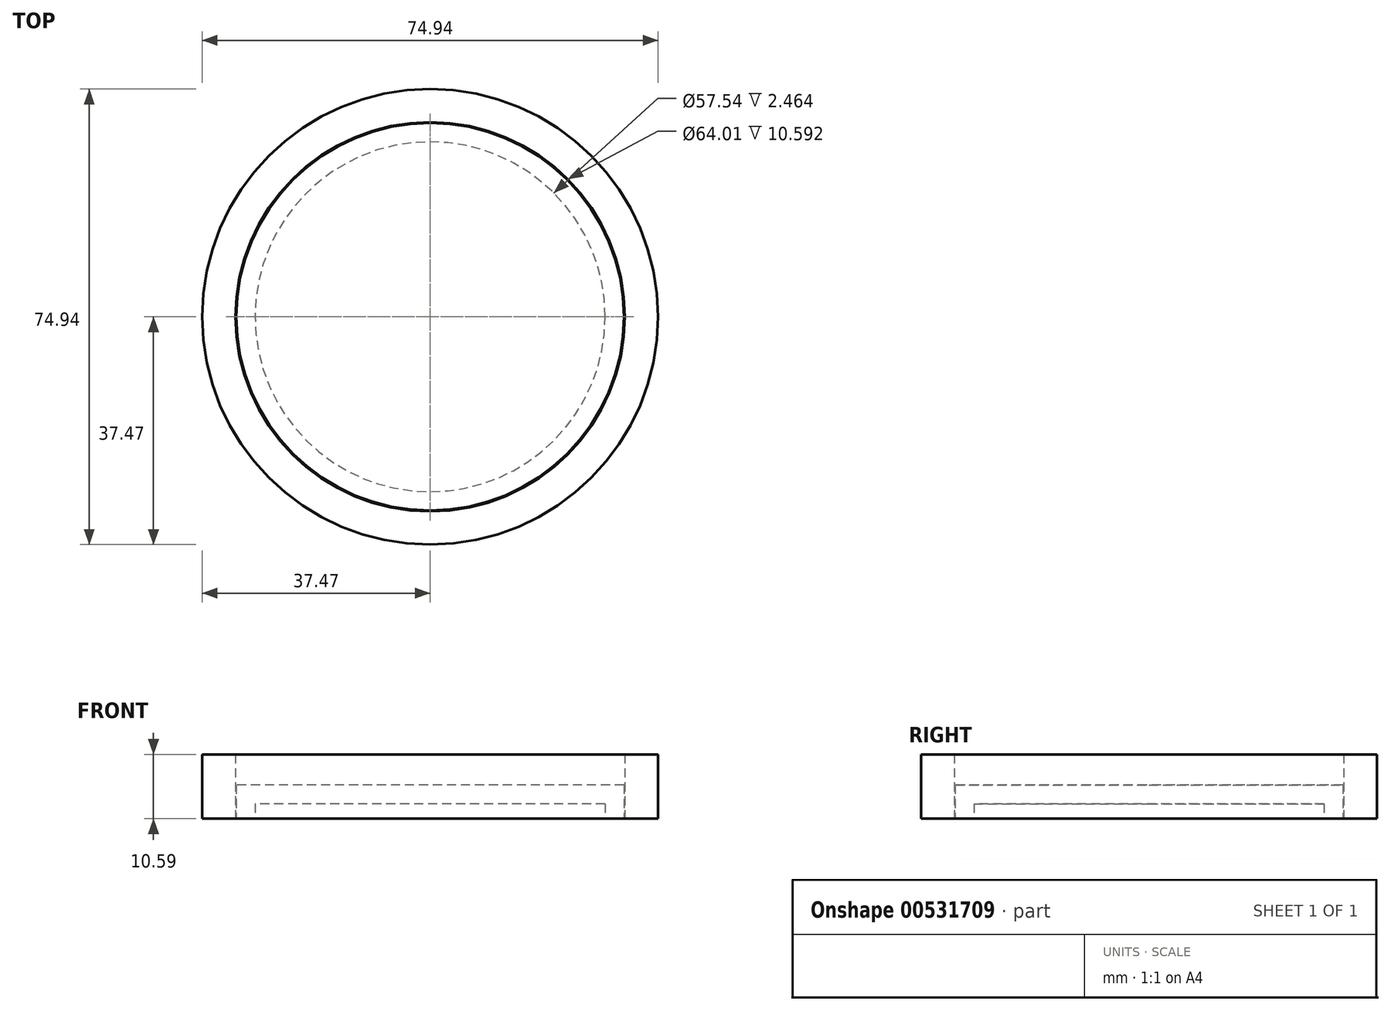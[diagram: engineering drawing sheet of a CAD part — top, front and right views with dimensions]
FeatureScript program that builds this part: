
annotation { "Feature Type Name" : "Feature", "Feature Type Description" : "" }
export const myFeature = defineFeature(function(context is Context, id is Id, definition is map)
    precondition{}
    {
        {
            var Q0;
            Q0=qCreatedBy(makeId("Top.planeOp"),FACE);
            var sketch = newSketch(context, id + "F0", { "sketchPlane" : qUnion([Q0])});
            skCircle(sketch, "E0", {"center": v(0, 0) * mm, "radius": 32 * mm});
            skCircle(sketch, "E1", {"center": v(0, 0) * mm, "radius": 37.47 * mm});
            skSolve(sketch);
        }
        {
            var Q0;
            Q0=makeQuery(id+"F0.imprint","IMPRINT",FACE,{"disambiguationData":[TD([[makeQuery(id+"F0.imprint","IMPRINT",EDGE,{"derivedFrom":sQuery(id+"F0.wireOp",EDGE,"E0")}),-1.0]])]});
            extrude(context, id + "F1", {"entities" : qUnion([Q0]), "depth" : 10.6 * mm, "offsetDistance" : 25.4 * mm});
        }
        {
            var Q0;
            Q0=qCreatedBy(makeId("Top.planeOp"),FACE);
            var sketch = newSketch(context, id + "F2", { "sketchPlane" : qUnion([Q0])});
            skCircle(sketch, "E2", {"center": v(0, 0) * mm, "radius": 31.87 * mm});
            skSolve(sketch);
        }
        {
            var Q0;
            Q0=makeQuery(id+"F2.imprint","IMPRINT",FACE,{"disambiguationData":[TD([[makeQuery(id+"F2.imprint","IMPRINT",EDGE,{"derivedFrom":sQuery(id+"F2.wireOp",EDGE,"E2")}),1.0]])]});
            extrude(context, id + "F3", {"entities" : qUnion([Q0]), "depth" : 5.56 * mm, "offsetDistance" : 25.4 * mm});
        }
        {
            var Q0;
            Q0=makeQuery(id+"F3.opExtrude","CAP_FACE",FACE,{"disambiguationData":[OSD([sQuery(id+"F2.wireOp",EDGE,"E2")])],"isStart":true});
            shell(context, id + "F4", {"entities" : qUnion([Q0]), "thickness" : 3.1 * mm});
        }
    });
